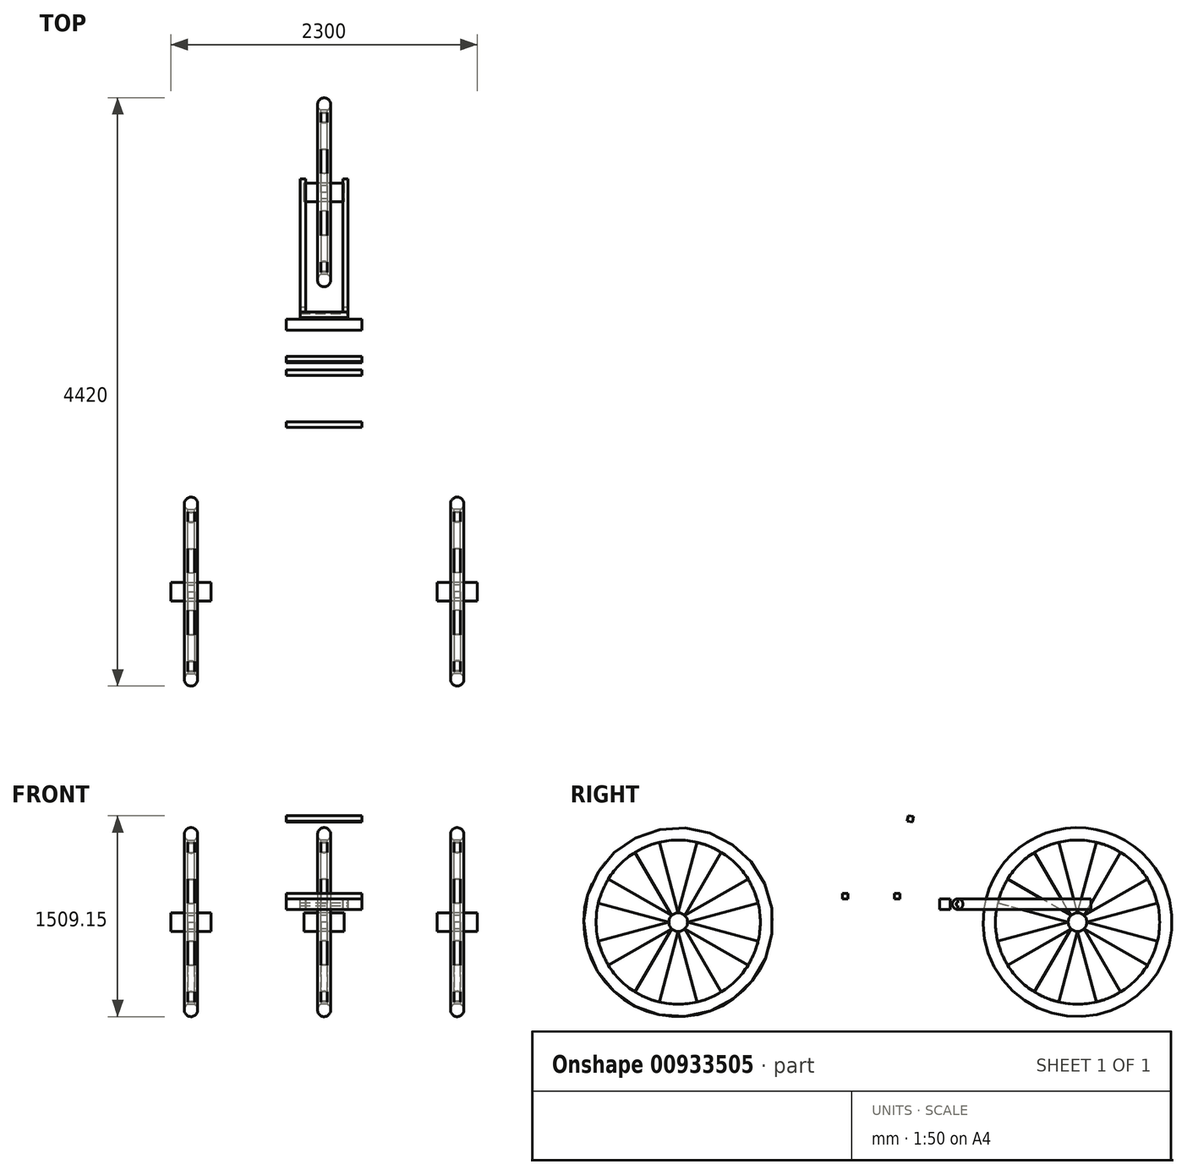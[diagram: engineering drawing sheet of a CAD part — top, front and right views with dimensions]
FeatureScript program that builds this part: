
annotation { "Feature Type Name" : "Feature", "Feature Type Description" : "" }
export const myFeature = defineFeature(function(context is Context, id is Id, definition is map)
    precondition{}
    {
        {
            var Q0;
            Q0=qCreatedBy(makeId("Top.planeOp"),FACE);
            var sketch = newSketch(context, id + "F0", { "sketchPlane" : qUnion([Q0])});
            skCircle(sketch, "E0", {"center": v(0, -660) * mm, "radius": 50 * mm});
            skLineSegment(sketch, "E1", {"start": v(49.25, 0) * mm, "end": v(-36.67, 0) * mm, "construction": true});
            skLineSegment(sketch, "E2", {"start": v(-150, 0) * mm, "end": v(150, 0) * mm});
            skLineSegment(sketch, "E3", {"start": v(-150, 0) * mm, "end": v(-150, -70) * mm});
            skLineSegment(sketch, "E4", {"start": v(-150, -70) * mm, "end": v(-25, -70) * mm});
            skLineSegment(sketch, "E5", {"start": v(-25, -70) * mm, "end": v(-25, -616.7) * mm});
            skLineSegment(sketch, "E6", {"start": v(150, 0) * mm, "end": v(150, -70) * mm});
            skLineSegment(sketch, "E7", {"start": v(150, -70) * mm, "end": v(25, -70) * mm});
            skLineSegment(sketch, "E8", {"start": v(25, -70) * mm, "end": v(25, -616.7) * mm});
            skSolve(sketch);
        }
        {
            var Q0;
            Q0=makeQuery(id+"F0.imprint","IMPRINT",FACE,{"disambiguationData":[TD([[makeQuery(id+"F0.imprint","IMPRINT",EDGE,{"derivedFrom":sQuery(id+"F0.wireOp",EDGE,"E0")}),1.0]])]});
            var Q1;
            Q1=sQuery(id+"F0.wireOp",EDGE,"E1");
            revolve(context, id + "F1", {"surfaceOperationType" : NewSurfaceOperationType.NEW, "entities" : qUnion([Q0]), "axis" : qUnion([Q1]), "revolveType" : RevolveType.FULL});
        }
        {
            var Q0;
            Q0=makeQuery(id+"F0.imprint","IMPRINT",FACE,{"disambiguationData":[TD([[makeQuery(id+"F0.imprint","IMPRINT",EDGE,{"derivedFrom":sQuery(id+"F0.wireOp",EDGE,"E2")}),-1.0]])]});
            var Q1;
            Q1=sQuery(id+"F0.wireOp",EDGE,"E2");
            revolve(context, id + "F2", {"surfaceOperationType" : NewSurfaceOperationType.NEW, "entities" : qUnion([Q0]), "axis" : qUnion([Q1]), "revolveType" : RevolveType.FULL});
        }
        {
            var Q0;
            Q0=makeQuery(id+"F2.opRevolve","SWEPT_FACE",FACE,{"disambiguationData":[OSD([sQuery(id+"F0.wireOp",EDGE,"E5")])]});
            var sketch = newSketch(context, id + "F3", { "sketchPlane" : qUnion([Q0])});
            skLineSegment(sketch, "E9", {"start": v(0, 70) * mm, "end": v(-142.04, 600.12) * mm});
            skLineSegment(sketch, "E10", {"start": v(0, 70) * mm, "end": v(142.04, 600.12) * mm});
            skLineSegment(sketch, "E11", {"start": v(0, 0) * mm, "end": v(0, 371.22) * mm, "construction": true});
            skLineSegment(sketch, "E12.1.0", {"start": v(-49.5, 49.5) * mm, "end": v(-323.9, 524.79) * mm});
            skLineSegment(sketch, "E12.1.1", {"start": v(-49.5, 49.5) * mm, "end": v(-524.79, 323.9) * mm});
            skLineSegment(sketch, "E12.1.2", {"start": v(0, 0) * mm, "end": v(-262.5, 262.5) * mm, "construction": true});
            skLineSegment(sketch, "E12.2.0", {"start": v(-70, 0) * mm, "end": v(-600.12, 142.04) * mm});
            skLineSegment(sketch, "E12.2.1", {"start": v(-70, 0) * mm, "end": v(-600.12, -142.04) * mm});
            skLineSegment(sketch, "E12.2.2", {"start": v(0, 0) * mm, "end": v(-371.22, 0) * mm, "construction": true});
            skPoint(sketch, "E12.center", {"position": v(0, 0) * mm});
            skLineSegment(sketch, "E13.1.3.0", {"start": v(-49.5, -49.5) * mm, "end": v(-524.79, -323.9) * mm});
            skLineSegment(sketch, "E13.3.3.0", {"start": v(-49.5, -49.5) * mm, "end": v(-323.9, -524.79) * mm});
            skLineSegment(sketch, "E13.6.3.0", {"start": v(0, 0) * mm, "end": v(-262.5, -262.5) * mm, "construction": true});
            skLineSegment(sketch, "E14.1.4.0", {"start": v(0, -70) * mm, "end": v(-142.04, -600.12) * mm});
            skLineSegment(sketch, "E14.3.4.0", {"start": v(0, -70) * mm, "end": v(142.04, -600.12) * mm});
            skLineSegment(sketch, "E14.6.4.0", {"start": v(0, 0) * mm, "end": v(0, -371.22) * mm, "construction": true});
            skLineSegment(sketch, "E15.1.5.0", {"start": v(49.5, -49.5) * mm, "end": v(323.9, -524.79) * mm});
            skLineSegment(sketch, "E15.3.5.0", {"start": v(49.5, -49.5) * mm, "end": v(524.79, -323.9) * mm});
            skLineSegment(sketch, "E15.6.5.0", {"start": v(0, 0) * mm, "end": v(262.5, -262.5) * mm, "construction": true});
            skLineSegment(sketch, "E16.1.6.0", {"start": v(70, 0) * mm, "end": v(600.12, -142.04) * mm});
            skLineSegment(sketch, "E16.3.6.0", {"start": v(70, 0) * mm, "end": v(600.12, 142.04) * mm});
            skLineSegment(sketch, "E16.6.6.0", {"start": v(0, 0) * mm, "end": v(371.22, 0) * mm, "construction": true});
            skLineSegment(sketch, "E16.1.7.0", {"start": v(49.5, 49.5) * mm, "end": v(524.79, 323.9) * mm});
            skLineSegment(sketch, "E16.3.7.0", {"start": v(49.5, 49.5) * mm, "end": v(323.9, 524.79) * mm});
            skLineSegment(sketch, "E16.6.7.0", {"start": v(0, 0) * mm, "end": v(262.5, 262.5) * mm, "construction": true});
            skSolve(sketch);
        }
        {
            var Q0;
            {var subQ0=sQuery(id+"F3.wireOp",EDGE,"E9");Q0=makeQuery(id+"F3.imprint","IMPRINT",FACE,{"disambiguationData":[TD([[makeQuery(id+"F3.imprint","IMPRINT",EDGE,{"derivedFrom":subQ0}),-1.0]])]});}
            var Q1;
            {var subQ0=sQuery(id+"F3.wireOp",EDGE,"E16.1.7.0");Q1=makeQuery(id+"F3.imprint","IMPRINT",FACE,{"disambiguationData":[TD([[makeQuery(id+"F3.imprint","IMPRINT",EDGE,{"derivedFrom":subQ0}),1.0]])]});}
            var Q2;
            {var subQ0=sQuery(id+"F3.wireOp",EDGE,"E16.1.6.0");Q2=makeQuery(id+"F3.imprint","IMPRINT",FACE,{"disambiguationData":[TD([[makeQuery(id+"F3.imprint","IMPRINT",EDGE,{"derivedFrom":subQ0}),1.0]])]});}
            var Q3;
            {var subQ0=sQuery(id+"F3.wireOp",EDGE,"E15.1.5.0");Q3=makeQuery(id+"F3.imprint","IMPRINT",FACE,{"disambiguationData":[TD([[makeQuery(id+"F3.imprint","IMPRINT",EDGE,{"derivedFrom":subQ0}),1.0]])]});}
            var Q4;
            {var subQ0=sQuery(id+"F3.wireOp",EDGE,"E14.1.4.0");Q4=makeQuery(id+"F3.imprint","IMPRINT",FACE,{"disambiguationData":[TD([[makeQuery(id+"F3.imprint","IMPRINT",EDGE,{"derivedFrom":subQ0}),1.0]])]});}
            var Q5;
            {var subQ0=sQuery(id+"F3.wireOp",EDGE,"E13.1.3.0");Q5=makeQuery(id+"F3.imprint","IMPRINT",FACE,{"disambiguationData":[TD([[makeQuery(id+"F3.imprint","IMPRINT",EDGE,{"derivedFrom":subQ0}),1.0]])]});}
            var Q6;
            {var subQ0=sQuery(id+"F3.wireOp",EDGE,"E12.2.0");Q6=makeQuery(id+"F3.imprint","IMPRINT",FACE,{"disambiguationData":[TD([[makeQuery(id+"F3.imprint","IMPRINT",EDGE,{"derivedFrom":subQ0}),1.0]])]});}
            var Q7;
            {var subQ0=sQuery(id+"F3.wireOp",EDGE,"E12.1.0");Q7=makeQuery(id+"F3.imprint","IMPRINT",FACE,{"disambiguationData":[TD([[makeQuery(id+"F3.imprint","IMPRINT",EDGE,{"derivedFrom":subQ0}),1.0]])]});}
            extrude(context, id + "F4", {"entities" : qUnion([Q0, Q1, Q2, Q3, Q4, Q5, Q6, Q7]), "operationType" : NewBodyOperationType.REMOVE, "endBound" : BoundingType.THROUGH_ALL, "oppositeDirection" : true, "depth" : 25 * mm, "offsetDistance" : 25 * mm});
        }
        {
            var Q0;
            Q0=qCreatedBy(makeId("Front.planeOp"),FACE);
            cPlane(context, id + "F5", {"entities" : qUnion([Q0]), "cplaneType" : CPlaneType.OFFSET, "offset" : 1500 * mm, "width" : 150 * mm, "height" : 150 * mm});
        }
        {
            var Q0;
            Q0=makeQuery(id+"F1.opRevolve","SWEPT_BODY",BODY,{"disambiguationData":[OSD([sQuery(id+"F0.wireOp",EDGE,"E0")])]});
            var Q1;
            Q1=makeQuery(id+"F2.opRevolve","SWEPT_BODY",BODY,{"disambiguationData":[OSD([sQuery(id+"F0.wireOp",EDGE,"E0"),sQuery(id+"F0.wireOp",EDGE,"E2"),sQuery(id+"F0.wireOp",EDGE,"E3"),sQuery(id+"F0.wireOp",EDGE,"E4"),sQuery(id+"F0.wireOp",EDGE,"E5"),sQuery(id+"F0.wireOp",EDGE,"E6"),sQuery(id+"F0.wireOp",EDGE,"E7"),sQuery(id+"F0.wireOp",EDGE,"E8")])]});
            var Q2;
            Q2=qCreatedBy(id+"F5.planeOp",FACE);
            mirror(context, id + "F6", {"entities" : qUnion([Q0, Q1]), "mirrorPlane" : qUnion([Q2])});
        }
        {
            var Q0;
            Q0=makeQuery(id+"F6.opPattern","COPY",BODY,{"derivedFrom":makeQuery(id+"F1.opRevolve","SWEPT_BODY",BODY,{"disambiguationData":[OSD([sQuery(id+"F0.wireOp",EDGE,"E0")])]}),"instanceName":"1"});
            var Q1;
            Q1=makeQuery(id+"F6.opPattern","COPY",BODY,{"derivedFrom":makeQuery(id+"F2.opRevolve","SWEPT_BODY",BODY,{"disambiguationData":[OSD([sQuery(id+"F0.wireOp",EDGE,"E0"),sQuery(id+"F0.wireOp",EDGE,"E2"),sQuery(id+"F0.wireOp",EDGE,"E3"),sQuery(id+"F0.wireOp",EDGE,"E4"),sQuery(id+"F0.wireOp",EDGE,"E5"),sQuery(id+"F0.wireOp",EDGE,"E6"),sQuery(id+"F0.wireOp",EDGE,"E7"),sQuery(id+"F0.wireOp",EDGE,"E8")])]}),"instanceName":"1"});
            var Q2;
            Q2=sQuery(id+"F0.wireOp",EDGE,"E2");
            var Q3;
            Q3=sQuery(id+"F0.wireOp",EDGE,"E2");
            transform(context, id + "F7", {"entities" : qUnion([Q0, Q1]), "transformType" : TransformType.TRANSLATION_DISTANCE, "transformDirection" : qUnion([Q3]), "distance" : 1000 * mm, "makeCopy" : false});
        }
        {
            var Q0;
            Q0=makeQuery(id+"F6.opPattern","COPY",BODY,{"derivedFrom":makeQuery(id+"F1.opRevolve","SWEPT_BODY",BODY,{"disambiguationData":[OSD([sQuery(id+"F0.wireOp",EDGE,"E0")])]}),"instanceName":"1"});
            var Q1;
            Q1=makeQuery(id+"F6.opPattern","COPY",BODY,{"derivedFrom":makeQuery(id+"F2.opRevolve","SWEPT_BODY",BODY,{"disambiguationData":[OSD([sQuery(id+"F0.wireOp",EDGE,"E0"),sQuery(id+"F0.wireOp",EDGE,"E2"),sQuery(id+"F0.wireOp",EDGE,"E3"),sQuery(id+"F0.wireOp",EDGE,"E4"),sQuery(id+"F0.wireOp",EDGE,"E5"),sQuery(id+"F0.wireOp",EDGE,"E6"),sQuery(id+"F0.wireOp",EDGE,"E7"),sQuery(id+"F0.wireOp",EDGE,"E8")])]}),"instanceName":"1"});
            var Q2;
            Q2=qCreatedBy(makeId("Right.planeOp"),FACE);
            mirror(context, id + "F8", {"entities" : qUnion([Q0, Q1]), "mirrorPlane" : qUnion([Q2])});
        }
        {
            var Q0;
            Q0=qCreatedBy(makeId("Front.planeOp"),FACE);
            var sketch = newSketch(context, id + "F9", { "sketchPlane" : qUnion([Q0])});
            skLineSegment(sketch, "E17.0", {"start": v(-150, -70) * mm, "end": v(-150, 70) * mm});
            skLineSegment(sketch, "E18.0", {"start": v(150, -70) * mm, "end": v(150, 70) * mm});
            skLineSegment(sketch, "E19", {"start": v(-218.43, 0) * mm, "end": v(160, 0) * mm, "construction": true});
            skLineSegment(sketch, "E20.bottom", {"start": v(140, 95) * mm, "end": v(180, 95) * mm});
            skLineSegment(sketch, "E20.top", {"start": v(140, 175) * mm, "end": v(180, 175) * mm});
            skLineSegment(sketch, "E20.left", {"start": v(140, 95) * mm, "end": v(140, 175) * mm});
            skLineSegment(sketch, "E20.right", {"start": v(180, 95) * mm, "end": v(180, 175) * mm});
            skPoint(sketch, "E20.middle", {"position": v(160, 135) * mm});
            skLineSegment(sketch, "E21", {"start": v(0, 0) * mm, "end": v(0, 190.68) * mm, "construction": true});
            skLineSegment(sketch, "E22.MirrorCS", {"start": v(-180, 95) * mm, "end": v(-180, 175) * mm});
            skPoint(sketch, "E23.MirrorP", {"position": v(-160, 135) * mm});
            skLineSegment(sketch, "E24.MirrorCS", {"start": v(-140, 95) * mm, "end": v(-140, 175) * mm});
            skLineSegment(sketch, "E25.MirrorCS", {"start": v(-140, 175) * mm, "end": v(-180, 175) * mm});
            skLineSegment(sketch, "E26.MirrorCS", {"start": v(-140, 95) * mm, "end": v(-180, 95) * mm});
            skSolve(sketch);
        }
        {
            var Q0;
            Q0=makeQuery(id+"F9.imprint","IMPRINT",FACE,{"disambiguationData":[TD([[makeQuery(id+"F9.imprint","IMPRINT",EDGE,{"derivedFrom":sQuery(id+"F9.wireOp",EDGE,"E20.bottom")}),1.0]])]});
            var Q1;
            Q1=makeQuery(id+"F9.imprint","IMPRINT",FACE,{"disambiguationData":[TD([[makeQuery(id+"F9.imprint","IMPRINT",EDGE,{"derivedFrom":sQuery(id+"F9.wireOp",EDGE,"E22.MirrorCS")}),-1.0]])]});
            extrude(context, id + "F10", {"entities" : qUnion([Q0, Q1]), "depth" : 900 * mm, "offsetDistance" : 25 * mm});
        }
        {
            var Q0;
            Q0=makeQuery(id+"F10.opExtrude","CAP_FACE",FACE,{"disambiguationData":[OSD([sQuery(id+"F9.wireOp",EDGE,"E20.bottom"),sQuery(id+"F9.wireOp",EDGE,"E20.top"),sQuery(id+"F9.wireOp",EDGE,"E20.left"),sQuery(id+"F9.wireOp",EDGE,"E20.right")])],"isStart":true});
            var Q1;
            Q1=makeQuery(id+"F10.opExtrude","CAP_FACE",FACE,{"disambiguationData":[OSD([sQuery(id+"F9.wireOp",EDGE,"E22.MirrorCS"),sQuery(id+"F9.wireOp",EDGE,"E24.MirrorCS"),sQuery(id+"F9.wireOp",EDGE,"E25.MirrorCS"),sQuery(id+"F9.wireOp",EDGE,"E26.MirrorCS")])],"isStart":true});
            extrude(context, id + "F11", {"entities" : qUnion([Q0, Q1]), "operationType" : NewBodyOperationType.ADD, "depth" : 100 * mm, "offsetDistance" : 25 * mm});
        }
        {
            var Q0;
            {var subQ0=sQuery(id+"F9.wireOp",EDGE,"E20.right");Q0=makeQuery(id+"F11.boolean.opBoolean","MERGE",FACE,{"derivedFrom":[makeQuery(id+"F10.opExtrude","SWEPT_FACE",FACE,{"disambiguationData":[OSD([subQ0])]}),makeQuery(id+"F11.opExtrude","SWEPT_FACE",FACE,{"disambiguationData":[OSD([subQ0])]})]});}
            var sketch = newSketch(context, id + "F12", { "sketchPlane" : qUnion([Q0])});
            skCircle(sketch, "E27", {"center": v(-900, 135) * mm, "radius": 40 * mm});
            skCircle(sketch, "E28", {"center": v(-900, 135) * mm, "radius": 12.5 * mm});
            skSolve(sketch);
        }
        {
            var Q0;
            {var subQ1=sQuery(id+"F9.wireOp",EDGE,"E20.right");var subQ3=makeQuery(id+"F10.opExtrude","CAP_EDGE",EDGE,{"disambiguationData":[OSD([subQ1])],"isStart":false});Q0=makeQuery(id+"F12.imprint","IMPRINT",FACE,{"disambiguationData":[TD([[makeQuery(id+"F12.imprint","IMPRINT",EDGE,{"derivedFrom":subQ3}),1.0]])]});}
            var Q1;
            {var subQ1=sQuery(id+"F9.wireOp",EDGE,"E20.right");var subQ3=makeQuery(id+"F10.opExtrude","CAP_EDGE",EDGE,{"disambiguationData":[OSD([subQ1])],"isStart":false});Q1=makeQuery(id+"F12.imprint","IMPRINT",FACE,{"disambiguationData":[TD([[makeQuery(id+"F12.imprint","IMPRINT",EDGE,{"derivedFrom":subQ3}),-1.0]])]});}
            var Q2;
            {var subQ0=sQuery(id+"F9.wireOp",EDGE,"E22.MirrorCS");Q2=makeQuery(id+"F11.boolean.opBoolean","MERGE",FACE,{"derivedFrom":[makeQuery(id+"F10.opExtrude","SWEPT_FACE",FACE,{"disambiguationData":[OSD([subQ0])]}),makeQuery(id+"F11.opExtrude","SWEPT_FACE",FACE,{"disambiguationData":[OSD([subQ0])]})]});}
            extrude(context, id + "F13", {"entities" : qUnion([Q0, Q1]), "endBound" : BoundingType.UP_TO_SURFACE, "oppositeDirection" : true, "depth" : 25 * mm, "endBoundEntityFace" : qUnion([Q2]), "offsetDistance" : 25 * mm});
        }
        {
            var Q0;
            {var subQ1=sQuery(id+"F9.wireOp",EDGE,"E20.right");var subQ3=makeQuery(id+"F10.opExtrude","CAP_EDGE",EDGE,{"disambiguationData":[OSD([subQ1])],"isStart":false});Q0=makeQuery(id+"F12.imprint","IMPRINT",FACE,{"disambiguationData":[TD([[makeQuery(id+"F12.imprint","IMPRINT",EDGE,{"derivedFrom":subQ3}),-1.0]])]});}
            var Q1;
            {var subQ0=sQuery(id+"F12.wireOp",EDGE,"E28");var subQ1=makeQuery(id+"F10.opExtrude","CAP_EDGE",EDGE,{"disambiguationData":[OSD([sQuery(id+"F9.wireOp",EDGE,"E20.right")])],"isStart":false});var subQ2=makeQuery(id+"F12.imprint","INTERSECT",VERTEX,{"disambiguationData":[OD(0.0)],"derivedFrom":[subQ1,subQ0]});Q1=makeQuery(id+"F12.imprint","IMPRINT",FACE,{"disambiguationData":[TD([[makeQuery(id+"F12.imprint","IMPRINT",EDGE,{"disambiguationData":[TD([[subQ2,-1.0]])],"derivedFrom":subQ0}),1.0]])]});}
            var Q2;
            {var subQ0=sQuery(id+"F9.wireOp",EDGE,"E22.MirrorCS");Q2=makeQuery(id+"F11.boolean.opBoolean","MERGE",FACE,{"derivedFrom":[makeQuery(id+"F10.opExtrude","SWEPT_FACE",FACE,{"disambiguationData":[OSD([subQ0])]}),makeQuery(id+"F11.opExtrude","SWEPT_FACE",FACE,{"disambiguationData":[OSD([subQ0])]})]});}
            extrude(context, id + "F14", {"entities" : qUnion([Q0, Q1]), "operationType" : NewBodyOperationType.REMOVE, "endBound" : BoundingType.UP_TO_SURFACE, "oppositeDirection" : true, "depth" : 25 * mm, "endBoundEntityFace" : qUnion([Q2]), "offsetDistance" : 25 * mm});
        }
        {
            var Q0;
            Q0=qCreatedBy(makeId("Right.planeOp"),FACE);
            var sketch = newSketch(context, id + "F15", { "sketchPlane" : qUnion([Q0])});
            skCircle(sketch, "E29.0", {"center": v(-900, 135) * mm, "radius": 40 * mm});
            skLineSegment(sketch, "E30.bottom", {"start": v(-1035, 175) * mm, "end": v(-955, 175) * mm});
            skLineSegment(sketch, "E30.top", {"start": v(-1035, 95) * mm, "end": v(-955, 95) * mm});
            skLineSegment(sketch, "E30.left", {"start": v(-1035, 175) * mm, "end": v(-1035, 95) * mm});
            skLineSegment(sketch, "E30.right", {"start": v(-955, 175) * mm, "end": v(-955, 95) * mm});
            skPoint(sketch, "E30.middle", {"position": v(-995, 135) * mm});
            skLineSegment(sketch, "E31", {"start": v(-1279.25, 759.76) * mm, "end": v(-1272.3, 799.15) * mm});
            skLineSegment(sketch, "E32", {"start": v(-1272.3, 799.15) * mm, "end": v(-1232.91, 792.2) * mm});
            skLineSegment(sketch, "E33", {"start": v(-1232.91, 792.2) * mm, "end": v(-1239.86, 752.81) * mm});
            skLineSegment(sketch, "E34", {"start": v(-1239.86, 752.81) * mm, "end": v(-1279.25, 759.76) * mm});
            skLineSegment(sketch, "E35", {"start": v(-1335, 175) * mm, "end": v(-1335, 215) * mm});
            skLineSegment(sketch, "E36", {"start": v(-1335, 215) * mm, "end": v(-1375, 215) * mm});
            skLineSegment(sketch, "E37", {"start": v(-1375, 215) * mm, "end": v(-1375, 175) * mm});
            skLineSegment(sketch, "E38", {"start": v(-1375, 175) * mm, "end": v(-1335, 175) * mm});
            skLineSegment(sketch, "E39", {"start": v(-1765, 175) * mm, "end": v(-1765, 215) * mm});
            skLineSegment(sketch, "E40", {"start": v(-1765, 215) * mm, "end": v(-1725, 215) * mm});
            skLineSegment(sketch, "E41", {"start": v(-1725, 215) * mm, "end": v(-1725, 175) * mm});
            skLineSegment(sketch, "E42", {"start": v(-1725, 175) * mm, "end": v(-1765, 175) * mm});
            skLineSegment(sketch, "E43", {"start": v(-1355, 215) * mm, "end": v(-1259.56, 756.29) * mm, "construction": true});
            skLineSegment(sketch, "E44", {"start": v(-3354.57, 175) * mm, "end": v(-2841.12, 175) * mm});
            skPoint(sketch, "E44.startSnap0", {"position": v(-1745, 175) * mm});
            skLineSegment(sketch, "E45", {"start": v(-2841.12, 175) * mm, "end": v(-2841.12, 83.25) * mm});
            skLineSegment(sketch, "E46", {"start": v(-2841.12, 83.25) * mm, "end": v(-3354.57, 83.25) * mm});
            skLineSegment(sketch, "E47", {"start": v(-3354.57, 83.25) * mm, "end": v(-3354.57, 175) * mm});
            skSolve(sketch);
        }
        {
            var Q0;
            Q0=makeQuery(id+"F15.imprint","IMPRINT",FACE,{"disambiguationData":[TD([[makeQuery(id+"F15.imprint","IMPRINT",EDGE,{"derivedFrom":sQuery(id+"F15.wireOp",EDGE,"E30.bottom")}),-1.0]])]});
            var Q1;
            Q1=makeQuery(id+"F15.imprint","IMPRINT",FACE,{"disambiguationData":[TD([[makeQuery(id+"F15.imprint","IMPRINT",EDGE,{"derivedFrom":sQuery(id+"F15.wireOp",EDGE,"E35")}),1.0]])]});
            var Q2;
            Q2=makeQuery(id+"F15.imprint","IMPRINT",FACE,{"disambiguationData":[TD([[makeQuery(id+"F15.imprint","IMPRINT",EDGE,{"derivedFrom":sQuery(id+"F15.wireOp",EDGE,"E39")}),-1.0]])]});
            var Q3;
            Q3=makeQuery(id+"F15.imprint","IMPRINT",FACE,{"disambiguationData":[TD([[makeQuery(id+"F15.imprint","IMPRINT",EDGE,{"derivedFrom":sQuery(id+"F15.wireOp",EDGE,"E31")}),-1.0]])]});
            extrude(context, id + "F16", {"entities" : qUnion([Q0, Q1, Q2, Q3]), "endBound" : BoundingType.SYMMETRIC, "depth" : 568 * mm, "offsetDistance" : 25 * mm});
        }
    });
